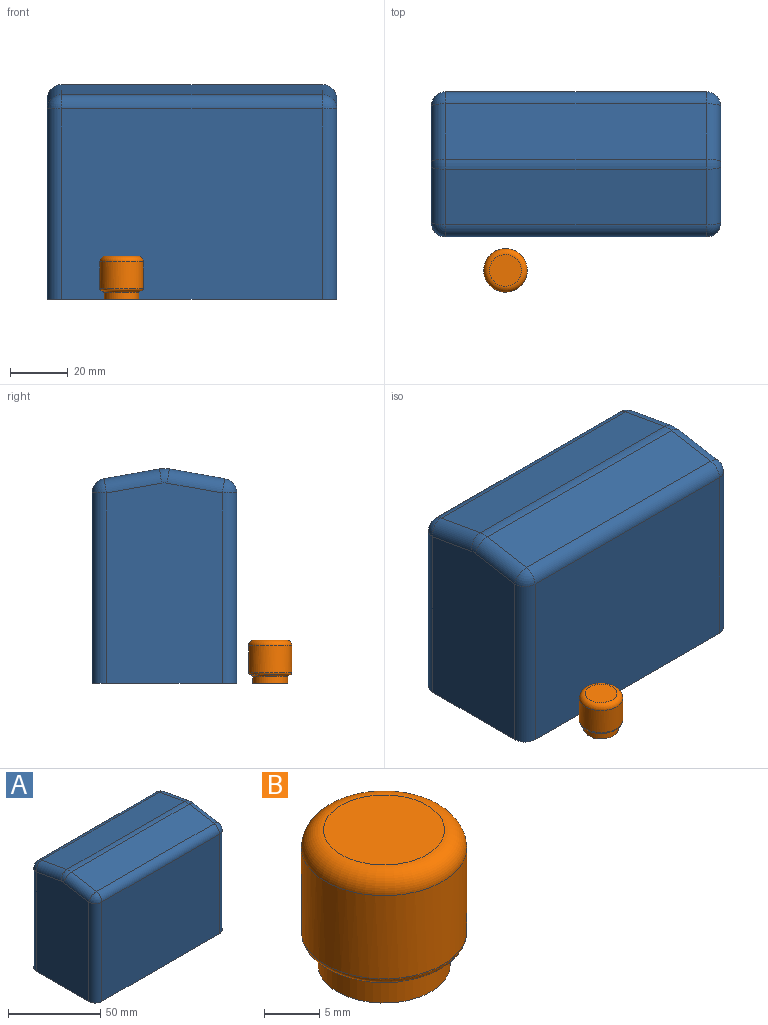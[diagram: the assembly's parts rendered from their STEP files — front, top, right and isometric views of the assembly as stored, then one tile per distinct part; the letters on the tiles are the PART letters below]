
ASSEMBLY  parts=2 mates=1
PART A: 47 faces, bbox 100x50x74.4 mm
  f0: plane 100x50mm, normal (0,0,-1), area 288.3mm2, adj f1,f2,f3,f4,f7,f8,f9,f10
  f1: plane 90x65.8mm, normal (0,-1,0), area 5922.4mm2, adj f0,f7,f10,f19
  f2: plane 69.25x40mm, normal (1,0,0), area 2702.7mm2, adj f0,f7,f8,f20,f22,f23
  f3: plane 90x65.8mm, normal (0,1,0), area 5922.4mm2, adj f0,f8,f9,f16
  f4: plane 69.25x40mm, normal (-1,0,0), area 2702.7mm2, adj f0,f9,f10,f12,f13,f15
  f5: plane 90x19.13mm, normal (0,-0.17,0.98), area 1748.4mm2, adj f11,f15,f19,f23
  f6: plane 90x19.13mm, normal (0,0.17,0.98), area 1748.4mm2, adj f11,f12,f16,f20
  f7: cylinder r=5mm len=65.8mm, axis (0,0,1), area 516.8mm2, adj f0,f1,f2,f21
  f8: cylinder r=5mm len=65.8mm, axis (0,0,-1), area 516.8mm2, adj f0,f2,f3,f18
  f9: cylinder r=5mm len=65.8mm, axis (0,0,1), area 516.8mm2, adj f0,f3,f4,f14
  f10: cylinder r=5mm len=65.8mm, axis (0,0,-1), area 516.8mm2, adj f0,f1,f4,f17
  f11: cylinder r=10mm len=90mm, axis (1,0,0), area 314.2mm2, adj f5,f6,f13,f22
  f12: cylinder r=5mm len=20mm, axis (0,-0.98,0.17), area 152.6mm2, adj f4,f6,f13,f14
  f13: torus R=5mm, axis (-1,0,0), area 22.4mm2, adj f4,f11,f12,f15
  f14: sphere r=5mm, area 34.9mm2, adj f9,f12,f16
  f15: cylinder r=5mm len=20mm, axis (0,-0.98,-0.17), area 152.6mm2, adj f4,f5,f13,f17
  f16: cylinder r=5mm len=90mm, axis (-1,0,0), area 628.3mm2, adj f3,f6,f14,f18
  f17: sphere r=5mm, area 34.9mm2, adj f10,f15,f19
  f18: sphere r=5mm, area 34.9mm2, adj f8,f16,f20
  f19: cylinder r=5mm len=90mm, axis (1,0,0), area 628.3mm2, adj f1,f5,f17,f21
  f20: cylinder r=5mm len=20mm, axis (0,0.98,-0.17), area 152.6mm2, adj f2,f6,f18,f22
  f21: sphere r=5mm, area 34.9mm2, adj f7,f19,f23
  f22: torus R=5mm, axis (-1,0,0), area 22.4mm2, adj f2,f11,f20,f23
  f23: cylinder r=5mm len=20mm, axis (0,0.98,0.17), area 152.6mm2, adj f2,f5,f21,f22
  f24: plane 90x65.8mm, normal (0,1,0), area 5922.4mm2, adj f0,f30,f33,f42
  f25: plane 69.25x40mm, normal (-1,0,0), area 2702.7mm2, adj f0,f30,f31,f43,f45,f46
  f26: plane 90x65.8mm, normal (0,-1,0), area 5922.4mm2, adj f0,f31,f32,f39
  f27: plane 69.25x40mm, normal (1,0,0), area 2702.7mm2, adj f0,f32,f33,f35,f36,f38
  f28: plane 90x19.13mm, normal (0,0.17,-0.98), area 1748.4mm2, adj f34,f38,f42,f46
  f29: plane 90x19.13mm, normal (0,-0.17,-0.98), area 1748.4mm2, adj f34,f35,f39,f43
  f30: cylinder r=4mm len=65.8mm, axis (0,0,1), area 413.5mm2, adj f0,f24,f25,f44
  f31: cylinder r=4mm len=65.8mm, axis (0,0,-1), area 413.5mm2, adj f0,f25,f26,f41
  f32: cylinder r=4mm len=65.8mm, axis (0,0,1), area 413.5mm2, adj f0,f26,f27,f37
  f33: cylinder r=4mm len=65.8mm, axis (0,0,-1), area 413.5mm2, adj f0,f24,f27,f40
  f34: cylinder r=9mm len=90mm, axis (1,0,0), area 282.7mm2, adj f28,f29,f36,f45
  f35: cylinder r=4mm len=19.83mm, axis (0,-0.98,0.17), area 122.1mm2, adj f27,f29,f36,f37
  f36: torus R=5mm, axis (-1,0,0), area 16.6mm2, adj f27,f34,f35,f38
  f37: sphere r=4mm, area 22.3mm2, adj f32,f35,f39
  f38: cylinder r=4mm len=19.83mm, axis (0,-0.98,-0.17), area 122.1mm2, adj f27,f28,f36,f40
  f39: cylinder r=4mm len=90mm, axis (-1,0,0), area 502.7mm2, adj f26,f29,f37,f41
  f40: sphere r=4mm, area 22.3mm2, adj f33,f38,f42
  f41: sphere r=4mm, area 22.3mm2, adj f31,f39,f43
  f42: cylinder r=4mm len=90mm, axis (1,0,0), area 502.7mm2, adj f24,f28,f40,f44
  f43: cylinder r=4mm len=19.83mm, axis (0,0.98,-0.17), area 122.1mm2, adj f25,f29,f41,f45
  f44: sphere r=4mm, area 22.3mm2, adj f30,f42,f46
  f45: torus R=5mm, axis (-1,0,0), area 16.6mm2, adj f25,f34,f43,f46
  f46: cylinder r=4mm len=19.83mm, axis (0,0.98,0.17), area 122.1mm2, adj f25,f28,f44,f45
PART B: 13 faces, bbox 16.5x16.5x15 mm
  f0: cylinder r=7.5mm len=15mm, axis (0,0,1), area 435.9mm2, adj f2,f5
  f1: plane 11x11mm, normal (0,0,1), area 95mm2, adj f2
  f2: torus R=5.5mm, axis (0,0,1), area 133.7mm2, adj f0,f1
  f3: cylinder r=6mm len=12mm, axis (0,0,-1), area 84.8mm2, adj f4,f6
  f4: plane 12x12mm, normal (0,0,-1), area 18.1mm2, adj f3,f10
  f5: torus R=6.75mm, axis (0,0,-1), area 53.5mm2, adj f0,f6
  f6: torus R=6.75mm, axis (0,0,-1), area 46.4mm2, adj f3,f5
  f7: cylinder r=7mm len=14mm, axis (0,0,1), area 406.8mm2, adj f9,f11
  f8: plane 11x11mm, normal (0,0,-1), area 95mm2, adj f9
  f9: torus R=5.5mm, axis (0,0,1), area 95.6mm2, adj f7,f8
  f10: cylinder r=5.5mm len=11mm, axis (0,0,-1), area 77.8mm2, adj f4,f12
  f11: torus R=6.75mm, axis (0,0,-1), area 17mm2, adj f7,f12
  f12: torus R=6.75mm, axis (0,0,-1), area 73.5mm2, adj f10,f11
PLACE A t=(-49.1,-50.25,-51.43)mm
PLACE B t=(-73.46,-52.32,-51.43)mm
MATE planar A.f0 <-> B.f0  axis (0,0,-1) through (-49.1,-50.25,-66.43)mm
